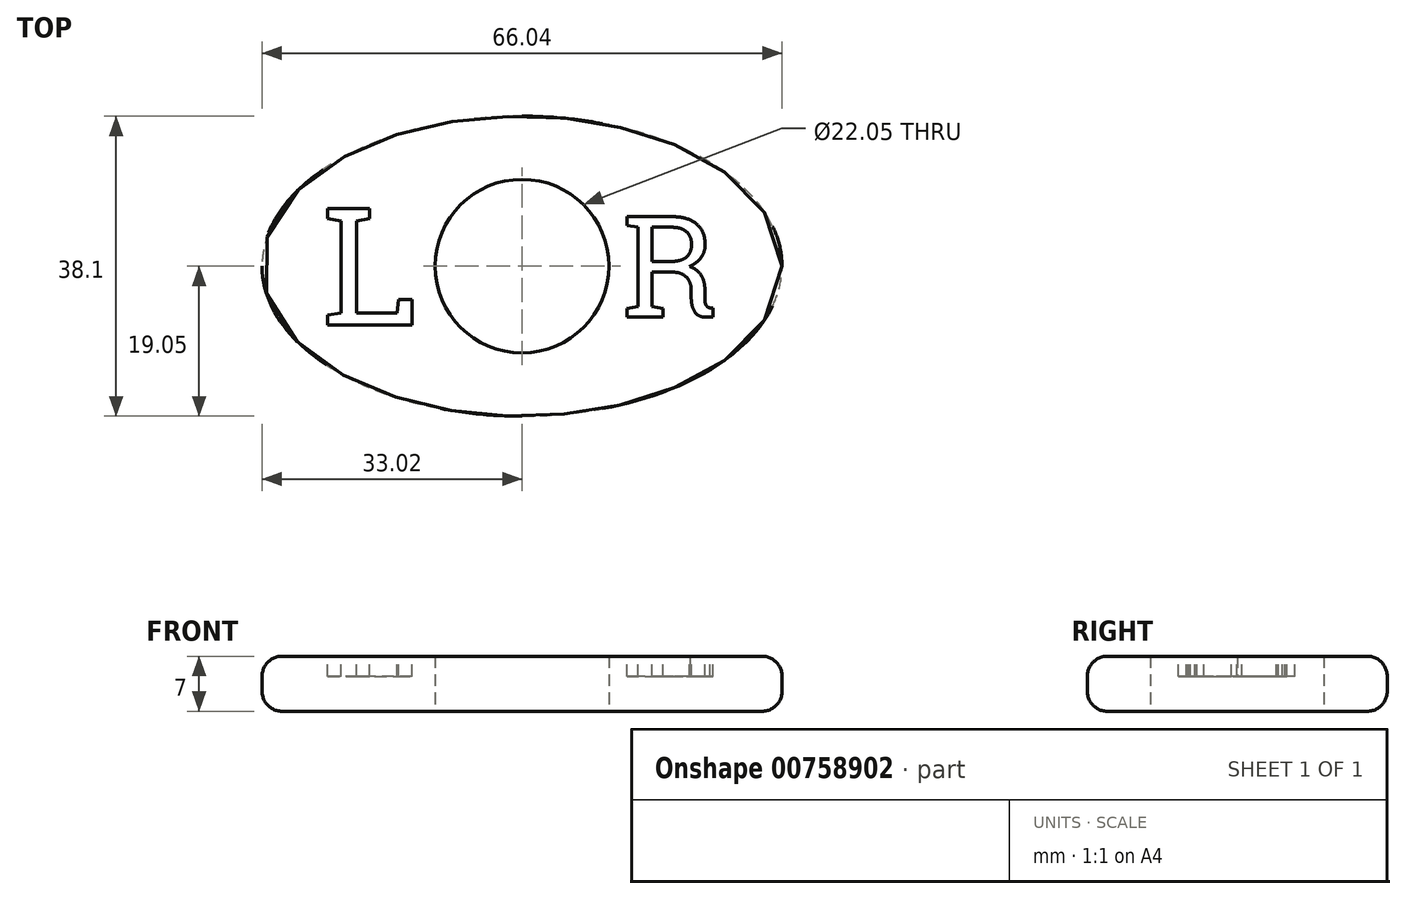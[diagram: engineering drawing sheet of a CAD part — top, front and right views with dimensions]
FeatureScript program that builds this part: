
annotation { "Feature Type Name" : "Feature", "Feature Type Description" : "" }
export const myFeature = defineFeature(function(context is Context, id is Id, definition is map)
    precondition{}
    {
        {
            var Q0;
            Q0=qCreatedBy(makeId("Top.planeOp"),FACE);
            var sketch = newSketch(context, id + "F0", { "sketchPlane" : qUnion([Q0])});
            skEllipse(sketch, "E0", {"center": v(0, 0) * mm, "majorRadius": 33.02 * mm, "minorRadius": 19.05 * mm, "majorAxis": v(1, 0)});
            skCircle(sketch, "E1", {"center": v(0, 0) * mm, "radius": 11.03 * mm});
            skLineSegment(sketch, "E2", {"start": v(-33.02, 0) * mm, "end": v(33.02, 0) * mm, "construction": true});
            skLineSegment(sketch, "E3", {"start": v(0, 19.05) * mm, "end": v(0, -19.05) * mm, "construction": true});
            skSolve(sketch);
        }
        {
            var Q0;
            Q0=makeQuery(id+"F0.imprint","IMPRINT",FACE,{"disambiguationData":[TD([[makeQuery(id+"F0.imprint","IMPRINT",EDGE,{"derivedFrom":sQuery(id+"F0.wireOp",EDGE,"E0")}),1.0]])]});
            extrude(context, id + "F1", {"entities" : qUnion([Q0]), "depth" : 7 * mm, "offsetDistance" : 25.4 * mm});
        }
        {
            var Q0;
            Q0=makeQuery(id+"F1.opExtrude","CAP_EDGE",EDGE,{"disambiguationData":[OSD([sQuery(id+"F0.wireOp",EDGE,"E0")])],"isStart":false});
            var Q1;
            Q1=makeQuery(id+"F1.opExtrude","CAP_EDGE",EDGE,{"disambiguationData":[OSD([sQuery(id+"F0.wireOp",EDGE,"E0")])],"isStart":true});
            fillet(context, id + "F2", {"entities" : qUnion([Q0, Q1]), "radius" : 2.54 * mm, "tangentPropagation" : true, "allowEdgeOverflow" : false});
        }
        {
            var Q0;
            Q0=makeQuery(id+"F1.opExtrude","CAP_FACE",FACE,{"disambiguationData":[OSD([sQuery(id+"F0.wireOp",EDGE,"E0"),sQuery(id+"F0.wireOp",EDGE,"E1")])],"isStart":false});
            var sketch = newSketch(context, id + "F3", { "sketchPlane" : qUnion([Q0])});
            skSolve(sketch);
        }
        {
            var Q0;
            {var subQ0=sQuery(id+"F0.wireOp",EDGE,"E1");Q0=makeQuery(id+"F3.imprint","IMPRINT",FACE,{"disambiguationData":[TD([[makeQuery(id+"F3.imprint","IMPRINT",EDGE,{"derivedFrom":makeQuery(id+"F1.opExtrude","CAP_EDGE",EDGE,{"disambiguationData":[OSD([subQ0])],"isStart":false})}),-1.0]])]});}
            var sketch = newSketch(context, id + "F4", { "sketchPlane" : qUnion([Q0])});
            skText(sketch, "E4", { "text": "L", "fontName": "RobotoSlab-Regular.ttf"});
            skText(sketch, "E5", { "text": "R", "fontName": "RobotoSlab-Regular.ttf"});
            skLineSegment(sketch, "E6", {"start": v(0, 0) * mm, "end": v(-25.4, 0) * mm, "construction": true});
            skLineSegment(sketch, "E7", {"start": v(0, 0) * mm, "end": v(25.4, 0) * mm, "construction": true});
            skLineSegment(sketch, "E8", {"start": v(-25.4, 0) * mm, "end": v(-12.7, 0) * mm, "construction": true});
            skLineSegment(sketch, "E9", {"start": v(12.7, 0) * mm, "end": v(25.4, 0) * mm});
            skPoint(sketch, "E10", {"position": v(19.05, 0) * mm});
            skLineSegment(sketch, "E11", {"start": v(12.7, 0) * mm, "end": v(25.4, 0) * mm, "construction": true});
            skPoint(sketch, "E12", {"position": v(-19.05, 0) * mm});
            const initialGuessF4  = {"E4": [-0.0254, -0.0075, 1, 0, 0.01502], "E5": [0.0127, -0.00648, 1, 0, 0.01295]};
            skSetInitialGuess(sketch, initialGuessF4);
            skSolve(sketch);
        }
        {
            var Q0;
            Q0=qSketchRegion(id+"F4",true);
            extrude(context, id + "F5", {"entities" : qUnion([Q0]), "operationType" : NewBodyOperationType.REMOVE, "oppositeDirection" : true, "depth" : 2.54 * mm, "offsetDistance" : 25.4 * mm});
        }
    });
